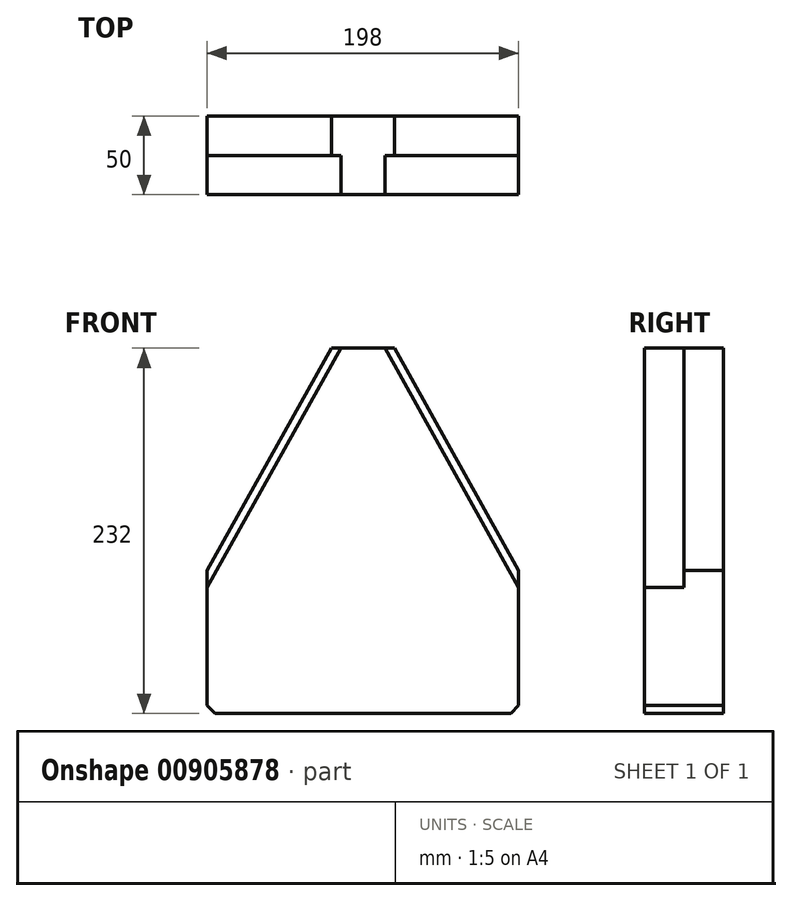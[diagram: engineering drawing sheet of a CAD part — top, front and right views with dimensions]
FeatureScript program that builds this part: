
annotation { "Feature Type Name" : "Feature", "Feature Type Description" : "" }
export const myFeature = defineFeature(function(context is Context, id is Id, definition is map)
    precondition{}
    {
        {
            var Q0;
            Q0=qCreatedBy(makeId("Front.planeOp"),FACE);
            var sketch = newSketch(context, id + "F0", { "sketchPlane" : qUnion([Q0])});
            skLineSegment(sketch, "E0.bottom", {"start": v(94, -116) * mm, "end": v(-94, -116) * mm});
            skLineSegment(sketch, "E0.top", {"start": v(20, 116) * mm, "end": v(-20, 116) * mm});
            skLineSegment(sketch, "E0.left", {"start": v(99, -111) * mm, "end": v(99, -30) * mm});
            skLineSegment(sketch, "E0.right", {"start": v(-99, -111) * mm, "end": v(-99, -30) * mm});
            skPoint(sketch, "E0.middle", {"position": v(0, 0) * mm});
            skLineSegment(sketch, "E1", {"start": v(0, 116) * mm, "end": v(-20, 116) * mm});
            skLineSegment(sketch, "E2", {"start": v(0, 116) * mm, "end": v(20, 116) * mm});
            skPoint(sketch, "E3.orphan", {"position": v(-99, 116) * mm});
            skPoint(sketch, "E4.orphan", {"position": v(99, 116) * mm});
            skLineSegment(sketch, "E5.top", {"start": v(-99, -111) * mm, "end": v(-94, -111) * mm});
            skLineSegment(sketch, "E5.right", {"start": v(-94, -116) * mm, "end": v(-94, -111) * mm});
            skLineSegment(sketch, "E6.top", {"start": v(99, -111) * mm, "end": v(94, -111) * mm});
            skLineSegment(sketch, "E6.right", {"start": v(94, -116) * mm, "end": v(94, -111) * mm});
            skLineSegment(sketch, "E7", {"start": v(-94, -116) * mm, "end": v(-99, -111) * mm});
            skLineSegment(sketch, "E8", {"start": v(94, -116) * mm, "end": v(99, -111) * mm});
            skPoint(sketch, "E9.orphan", {"position": v(99, -116) * mm});
            skPoint(sketch, "E10.orphan", {"position": v(-99, -116) * mm});
            skLineSegment(sketch, "E11", {"start": v(0, 116) * mm, "end": v(-14, 116) * mm});
            skLineSegment(sketch, "E12", {"start": v(-99, -111) * mm, "end": v(-99, -36) * mm});
            skLineSegment(sketch, "E13", {"start": v(-99, -36) * mm, "end": v(-14, 116) * mm});
            skLineSegment(sketch, "E14", {"start": v(0, 116) * mm, "end": v(14, 116) * mm});
            skLineSegment(sketch, "E15", {"start": v(14, 116) * mm, "end": v(99, -36) * mm});
            skLineSegment(sketch, "E16", {"start": v(99, -36) * mm, "end": v(99, -25) * mm});
            skLineSegment(sketch, "E17", {"start": v(99, -25) * mm, "end": v(20, 116) * mm});
            skLineSegment(sketch, "E18", {"start": v(-99, -36) * mm, "end": v(-99, -25) * mm});
            skLineSegment(sketch, "E19", {"start": v(-99, -25) * mm, "end": v(-20, 116) * mm});
            skSolve(sketch);
        }
        {
            var Q0;
            Q0 = qSketchRegion(id + "F0", true);
            extrude(context, id + "F1", {"entities" : qUnion([Q0]), "depth" : 25 * mm, "offsetDistance" : 25 * mm});
        }
        {
            var Q0;
            Q0=makeQuery(id+"F1.opExtrude","CAP_FACE",FACE,{"disambiguationData":[OSD([sQuery(id+"F0.wireOp",EDGE,"E0.bottom"),sQuery(id+"F0.wireOp",EDGE,"E0.left"),sQuery(id+"F0.wireOp",EDGE,"E0.right"),sQuery(id+"F0.wireOp",EDGE,"E1"),sQuery(id+"F0.wireOp",EDGE,"JP5q5w7k-NyZw-uimb-7eCg-ObjYanuekp6J"),sQuery(id+"F0.wireOp",EDGE,"E2"),sQuery(id+"F0.wireOp",EDGE,"jXezJ7Vd-HgIe-LC5d-AiFp-NPrV7SZ093wj"),sQuery(id+"F0.wireOp",EDGE,"E7"),sQuery(id+"F0.wireOp",EDGE,"E8"),sQuery(id+"F0.wireOp",EDGE,"E11"),sQuery(id+"F0.wireOp",EDGE,"E12"),sQuery(id+"F0.wireOp",EDGE,"E14")])],"isStart":false});
            var sketch = newSketch(context, id + "F2", { "sketchPlane" : qUnion([Q0])});
            skLineSegment(sketch, "E20", {"start": v(0, 116) * mm, "end": v(-14, 116) * mm});
            skLineSegment(sketch, "E21", {"start": v(-14, 116) * mm, "end": v(14, 116) * mm});
            skLineSegment(sketch, "E22", {"start": v(-99, -116) * mm, "end": v(-99, -36) * mm});
            skLineSegment(sketch, "E23", {"start": v(-99, -36) * mm, "end": v(-14, 116) * mm});
            skLineSegment(sketch, "E24", {"start": v(14, 116) * mm, "end": v(99, -36) * mm});
            skSolve(sketch);
        }
        {
            var Q0;
            Q0 = qSketchRegion(id + "F2", true);
            var Q1;
            {var subQ1=sQuery(id+"F2.wireOp",EDGE,"E23");Q1=makeQuery(id+"F2.imprint","IMPRINT",FACE,{"disambiguationData":[TD([[makeQuery(id+"F2.imprint","IMPRINT",EDGE,{"derivedFrom":subQ1}),-1.0]])]});}
            extrude(context, id + "F3", {"entities" : qUnion([Q0, Q1]), "operationType" : NewBodyOperationType.ADD, "depth" : 25 * mm, "offsetDistance" : 25 * mm});
        }
    });
